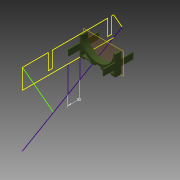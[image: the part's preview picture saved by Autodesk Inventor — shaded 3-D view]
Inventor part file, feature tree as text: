
AUTODESK INVENTOR PART (.ipt)
format: ipt  version: 2013 (Build 170138000, 138)  size: 315,392 bytes
history: native  units: mm
features: sketch x17, extrude x16, other x2
ambient origin geometry x8: Origin, YZ Plane, XZ Plane, XY Plane, X Axis, Y Axis, Z Axis, Center Point
feature tree (35):
  other  "ソリッド1"
  extrude  "押し出し1"  Depth=90.0mm
  extrude  "押し出し2"  Depth=50.0mm
  extrude  "押し出し3"  Depth=5.0mm
  extrude  "押し出し4"  Depth=85.0mm
  extrude  "押し出し6"  Depth=5.0mm
  sketch  "スケッチ9"
  extrude  "押し出し8"  Depth=80.0mm
  extrude  "押し出し9"  Depth=10.0mm
  extrude  "押し出し10"  Depth=90.0mm
  extrude  "押し出し11"  Depth=230.0mm TaperAngle=0.0deg
  extrude  "押し出し12"  Depth=225.0mm TaperAngle=0.0deg
  extrude  "押し出し13"  Depth=5.0mm TaperAngle=0.0deg
  extrude  "押し出し14"  Depth=65.0mm
  extrude  "押し出し15"  Depth=10.0mm
  other  "作業平面2"
  extrude  "押し出し16"  Depth=140.0mm
  extrude  "押し出し17"  Depth=10.0mm
  extrude  "押し出し18"  Depth=40.0mm
  sketch  "スケッチ1"
  sketch  "スケッチ2"
  sketch  "スケッチ3"
  sketch  "スケッチ4"
  sketch  "スケッチ6"
  sketch  "スケッチ12"
  sketch  "スケッチ13"
  sketch  "スケッチ14"
  sketch  "スケッチ16"
  sketch  "スケッチ17"
  sketch  "スケッチ18"
  sketch  "スケッチ19"
  sketch  "スケッチ20"
  sketch  "スケッチ21"
  sketch  "スケッチ22"
  sketch  "スケッチ23"
